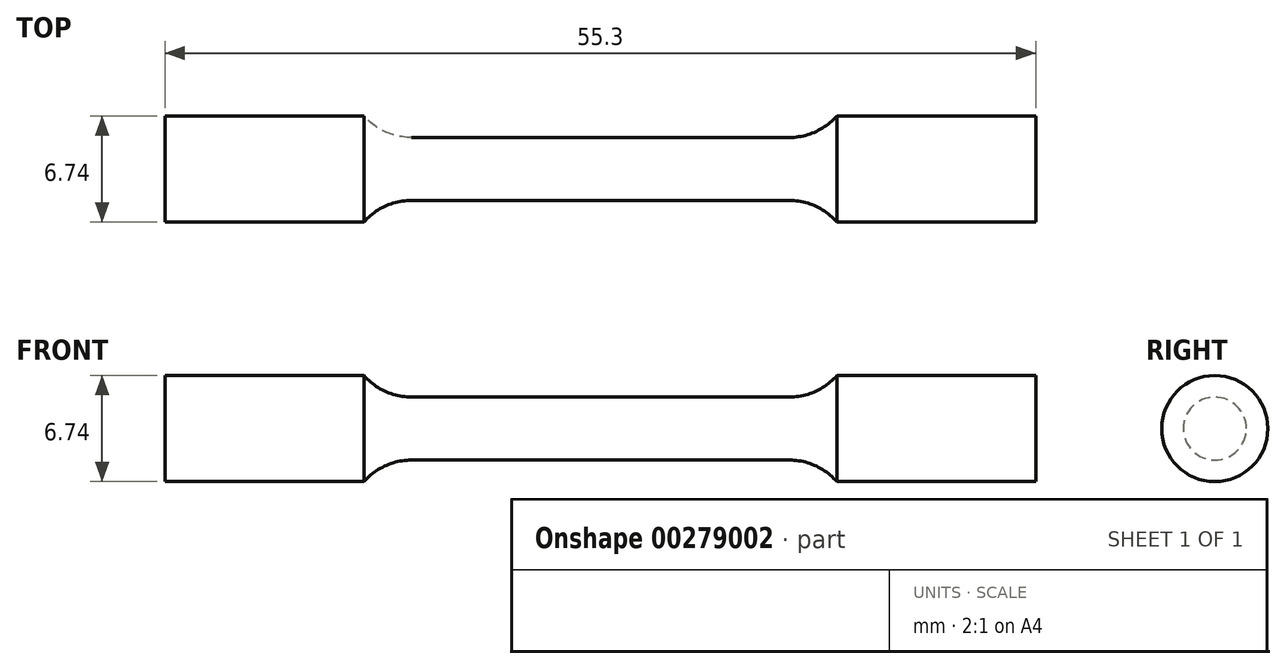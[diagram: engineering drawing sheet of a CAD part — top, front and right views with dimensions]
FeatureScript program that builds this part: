
annotation { "Feature Type Name" : "Feature", "Feature Type Description" : "" }
export const myFeature = defineFeature(function(context is Context, id is Id, definition is map)
    precondition{}
    {
        {
            var Q0;
            Q0=qCreatedBy(makeId("Front.planeOp"),FACE);
            var sketch = newSketch(context, id + "F0", { "sketchPlane" : qUnion([Q0])});
            skLineSegment(sketch, "E0", {"start": v(0, 2) * mm, "end": v(12, 2) * mm});
            skArc(sketch, "E1", {"start": v(12, 2) * mm, "mid": v(13.66, 2.36) * mm, "end": v(15.01, 3.37) * mm});
            skLineSegment(sketch, "E2", {"start": v(15.01, 3.37) * mm, "end": v(27.65, 3.37) * mm});
            skLineSegment(sketch, "E3", {"start": v(27.65, 3.37) * mm, "end": v(27.65, 0) * mm});
            skLineSegment(sketch, "E4.MirrorCS", {"start": v(0, 2) * mm, "end": v(-12, 2) * mm});
            skLineSegment(sketch, "E5.MirrorCS", {"start": v(-27.65, 3.37) * mm, "end": v(-27.65, 0) * mm});
            skLineSegment(sketch, "E6.MirrorCS", {"start": v(-15.01, 3.37) * mm, "end": v(-27.65, 3.37) * mm});
            skArc(sketch, "E7.MirrorCS", {"start": v(-12, 2) * mm, "mid": v(-13.66, 2.36) * mm, "end": v(-15.01, 3.37) * mm});
            skLineSegment(sketch, "E8", {"start": v(-27.65, 0) * mm, "end": v(27.65, 0) * mm});
            skSolve(sketch);
        }
        {
            var Q0;
            Q0=makeQuery(id+"F0.imprint","IMPRINT",FACE,{"disambiguationData":[TD([[makeQuery(id+"F0.imprint","IMPRINT",EDGE,{"derivedFrom":sQuery(id+"F0.wireOp",EDGE,"E0")}),-1.0]])]});
            var Q1;
            Q1=sQuery(id+"F0.wireOp",EDGE,"E8");
            revolve(context, id + "F1", {"entities" : qUnion([Q0]), "axis" : qUnion([Q1]), "revolveType" : RevolveType.FULL});
        }
    });
